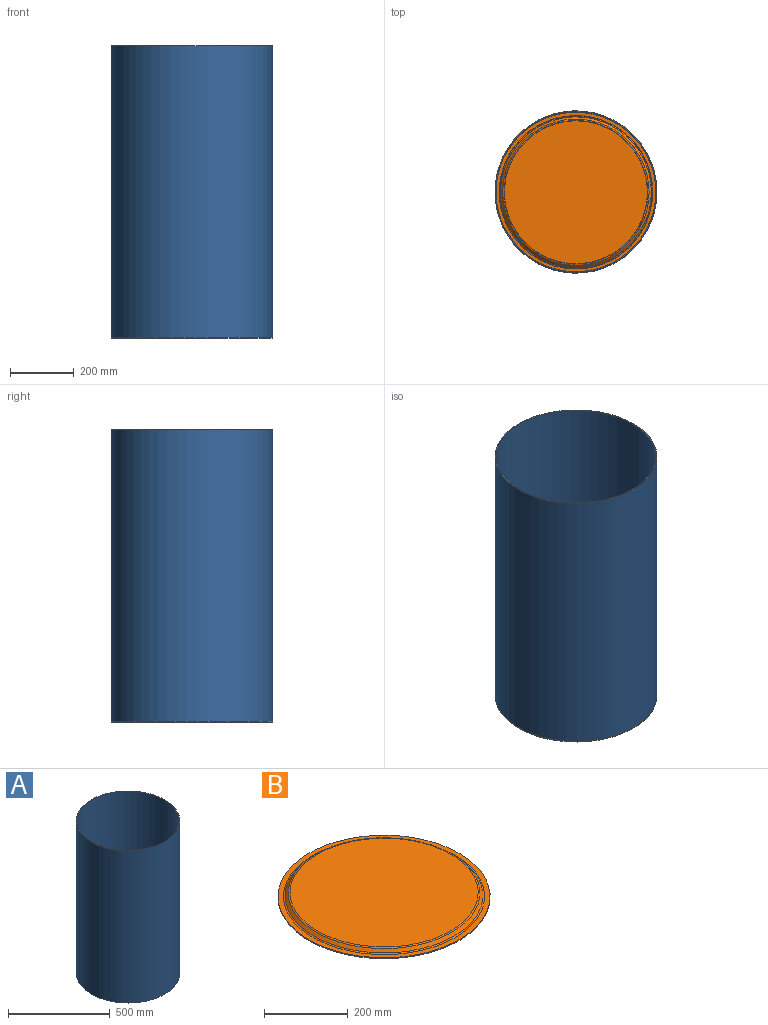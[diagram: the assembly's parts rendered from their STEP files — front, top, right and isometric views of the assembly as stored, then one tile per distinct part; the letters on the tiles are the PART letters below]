
ASSEMBLY  parts=2 mates=1
PART A: 4 faces, bbox 508x508x914.4 mm
  f0: cylinder r=250.83mm len=914.4mm, axis (0,0,-1), area 1441076.1mm2, adj f2,f3
  f1: cylinder r=254mm len=914.4mm, axis (0,0,-1), area 1459317.5mm2, adj f2,f3
  f2: plane 508x508mm, normal (0,0,1), area 5035.4mm2, adj f0,f1
  f3: plane 508x508mm, normal (0,0,-1), area 5035.4mm2, adj f0,f1
PART B: 11 faces, bbox 530.2x530.2x14.3 mm
  f0: torus R=239.69mm, axis (0,0,1), area 6988.9mm2, adj f1,f10
  f1: plane 508x508mm, normal (0,0,-1), area 22189.7mm2, adj f0,f2
  f2: cylinder r=254mm len=508mm, axis (0,0,1), area 4497.5mm2, adj f1,f3
  f3: plane 508x508mm, normal (0,0,1), area 20312.3mm2, adj f2,f4
  f4: torus R=240.94mm, axis (0,0,1), area 7025.5mm2, adj f3,f5
  f5: cone r=229.61mm half-angle=42.4deg, axis (0,0,-1), area 15569.3mm2, adj f4,f6
  f6: torus R=225.45mm, axis (0,0,1), area 6699.7mm2, adj f5,f7
  f7: plane 450.89x450.89mm, normal (0,0,1), area 159675.9mm2, adj f6
  f8: plane 448.41x448.41mm, normal (0,0,-1), area 157919.5mm2, adj f9
  f9: torus R=224.2mm, axis (0,0,1), area 6663.2mm2, adj f8,f10
  f10: cone r=228.37mm half-angle=42.4deg, axis (0,0,-1), area 15486.3mm2, adj f0,f9
PLACE A at identity
PLACE B t=(0,0,11.52)mm
MATE fastened B.f0 <-> A.f0  axis (0,0,1) through (0,0,0)mm
